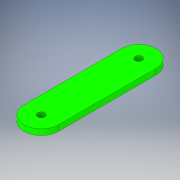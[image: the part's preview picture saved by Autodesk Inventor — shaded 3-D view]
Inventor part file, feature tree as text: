
AUTODESK INVENTOR PART (.ipt)
format: ipt  version: 2017 (Build 210142000, 142)  size: 117,248 bytes
history: native  units: in
note: dims shown in document units (in); Inventor stores cm internally (conversion verified against a paired STEP export)
features: extrude x1, sketch x1
ambient origin geometry x8: Origin, YZ Plane, XZ Plane, XY Plane, X Axis, Y Axis, Z Axis, Center Point
bodies: Solid1 (feature_tree)
feature tree (2):
  extrude  "Extrusion1"  Depth=0.75in
  sketch  "Sketch1"  dims[d0=1.5in d2=0.75in d6=0.0in]
